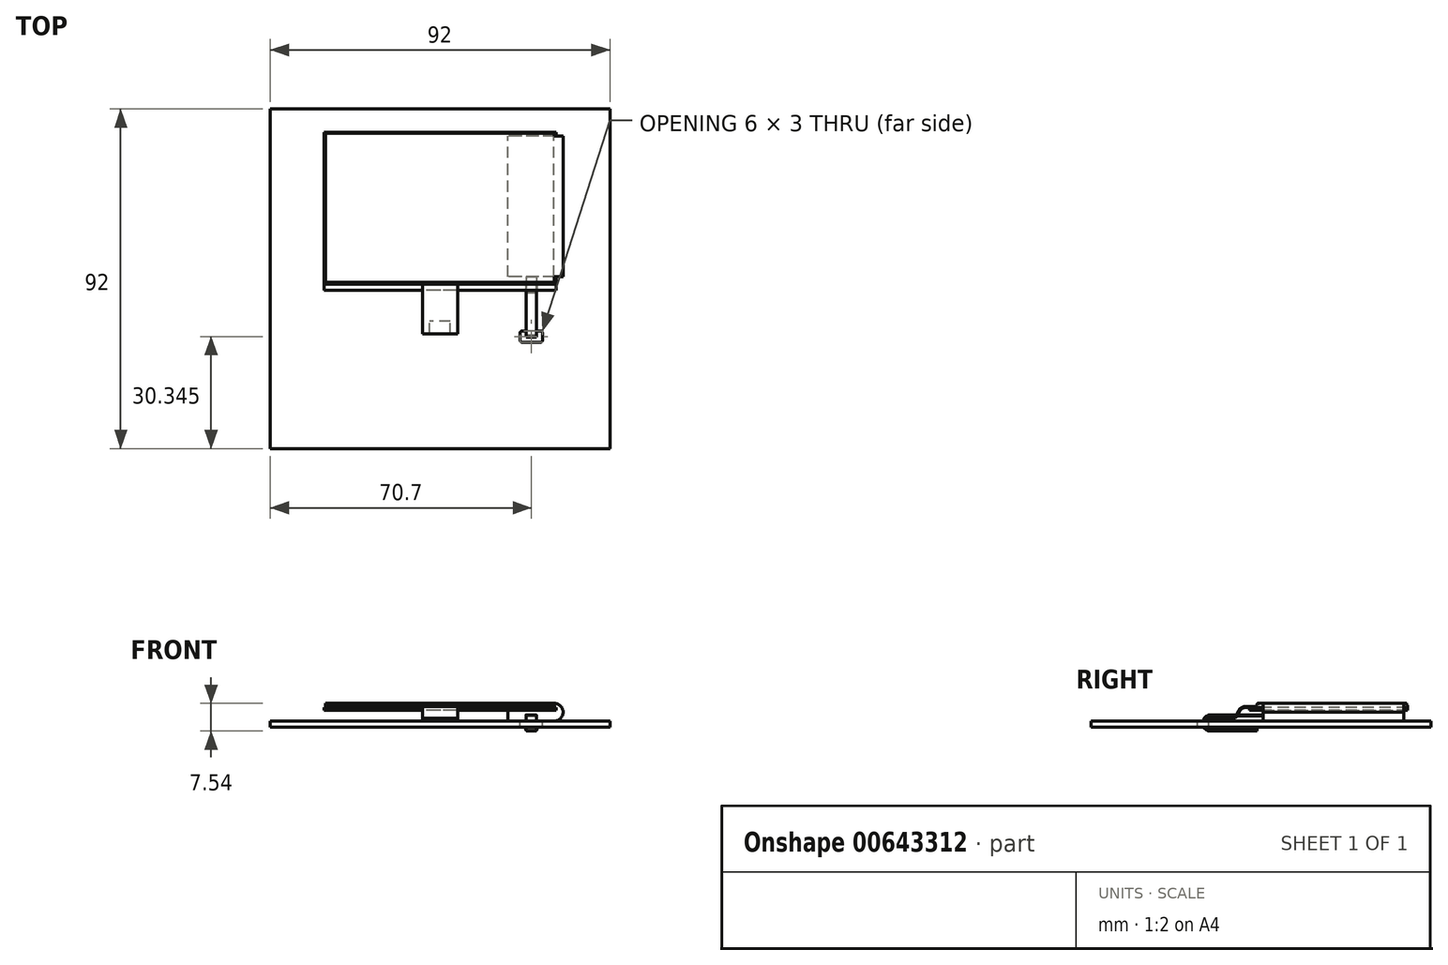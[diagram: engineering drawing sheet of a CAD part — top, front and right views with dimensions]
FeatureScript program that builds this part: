
annotation { "Feature Type Name" : "Feature", "Feature Type Description" : "" }
export const myFeature = defineFeature(function(context is Context, id is Id, definition is map)
    precondition{}
    {
        {
            var Q0;
            Q0=qCreatedBy(makeId("Top.planeOp"),FACE);
            var sketch = newSketch(context, id + "F0", { "sketchPlane" : qUnion([Q0])});
            skLineSegment(sketch, "E0.bottom", {"start": v(31.4, 21.41) * mm, "end": v(-31.4, 21.41) * mm});
            skLineSegment(sketch, "E0.top", {"start": v(31.4, -21.41) * mm, "end": v(-31.4, -21.41) * mm});
            skLineSegment(sketch, "E0.left", {"start": v(31.4, 21.41) * mm, "end": v(31.4, -21.41) * mm});
            skLineSegment(sketch, "E0.right", {"start": v(-31.4, 21.41) * mm, "end": v(-31.4, -21.41) * mm});
            skPoint(sketch, "E0.middle", {"position": v(0, 0) * mm});
            skSolve(sketch);
        }
        {
            var Q0;
            Q0=makeQuery(id+"F0.imprint","IMPRINT",FACE,{"disambiguationData":[TD([[makeQuery(id+"F0.imprint","IMPRINT",EDGE,{"derivedFrom":sQuery(id+"F0.wireOp",EDGE,"E0.bottom")}),1.0]])]});
            extrude(context, id + "F1", {"entities" : qUnion([Q0]), "depth" : (0.7 + 0.1) * mm, "offsetDistance" : 25 * mm});
        }
        {
            var Q0;
            Q0=makeQuery(id+"F1.opExtrude","CAP_FACE",FACE,{"disambiguationData":[OSD([sQuery(id+"F0.wireOp",EDGE,"E0.bottom"),sQuery(id+"F0.wireOp",EDGE,"E0.top"),sQuery(id+"F0.wireOp",EDGE,"E0.left"),sQuery(id+"F0.wireOp",EDGE,"E0.right")])],"isStart":true});
            var sketch = newSketch(context, id + "F2", { "sketchPlane" : qUnion([Q0])});
            skLineSegment(sketch, "E1.bottom", {"start": v(33.35, 17.74) * mm, "end": v(18.35, 17.74) * mm});
            skLineSegment(sketch, "E1.top", {"start": v(33.35, -20.41) * mm, "end": v(18.35, -20.41) * mm});
            skLineSegment(sketch, "E1.left", {"start": v(33.35, 17.74) * mm, "end": v(33.35, -20.41) * mm});
            skLineSegment(sketch, "E1.right", {"start": v(18.35, 17.74) * mm, "end": v(18.35, -20.41) * mm});
            skSolve(sketch);
        }
        {
            var Q0;
            Q0=qSketchRegion(id+"F2",true);
            extrude(context, id + "F3", {"entities" : qUnion([Q0]), "operationType" : NewBodyOperationType.ADD, "depth" : 2.9 * mm, "offsetDistance" : 25 * mm});
        }
        {
            var Q0;
            {var subQ0=sQuery(id+"F0.wireOp",EDGE,"E0.right");var subQ1=sQuery(id+"F0.wireOp",EDGE,"E0.left");var subQ2=sQuery(id+"F0.wireOp",EDGE,"E0.top");var subQ3=sQuery(id+"F0.wireOp",EDGE,"E0.bottom");Q0=makeQuery(id+"FSjtb73LsPTqSAc_1.boolean.opBoolean","MERGE",FACE,{"derivedFrom":[makeQuery(id+"F1.opExtrude","CAP_FACE",FACE,{"disambiguationData":[OSD([subQ3,subQ2,subQ1,subQ0])],"isStart":false}),makeQuery(id+"FSjtb73LsPTqSAc_1.opExtrude","CAP_FACE",FACE,{"disambiguationData":[OSD([subQ3,subQ2,subQ1,subQ0])],"isStart":false})]});}
            var sketch = newSketch(context, id + "F4", { "sketchPlane" : qUnion([Q0])});
            skLineSegment(sketch, "E2.bottom", {"start": v(-31, 21.4) * mm, "end": v(31, 21.41) * mm});
            skLineSegment(sketch, "E2.top", {"start": v(-31, -19.81) * mm, "end": v(31, -19.81) * mm});
            skLineSegment(sketch, "E2.left", {"start": v(-31, 21.4) * mm, "end": v(-31, -19.81) * mm});
            skLineSegment(sketch, "E2.right", {"start": v(31, 21.41) * mm, "end": v(31, -19.81) * mm});
            skLineSegment(sketch, "E3", {"start": v(0, 21.4) * mm, "end": v(0, -19.81) * mm, "construction": true});
            skSolve(sketch);
        }
        {
            var Q0;
            Q0=makeQuery(id+"F4.imprint","IMPRINT",FACE,{"disambiguationData":[TD([[makeQuery(id+"F4.imprint","IMPRINT",EDGE,{"derivedFrom":sQuery(id+"F4.wireOp",EDGE,"E2.bottom")}),1.0]])]});
            extrude(context, id + "F5", {"entities" : qUnion([Q0]), "operationType" : NewBodyOperationType.ADD, "depth" : 0.6 * mm, "offsetDistance" : 25 * mm});
        }
        {
            var Q0;
            Q0=makeQuery(id+"F5.opExtrude","CAP_FACE",FACE,{"disambiguationData":[OSD([sQuery(id+"F4.wireOp",EDGE,"E2.bottom"),sQuery(id+"F4.wireOp",EDGE,"E2.top"),sQuery(id+"F4.wireOp",EDGE,"E2.left"),sQuery(id+"F4.wireOp",EDGE,"E2.right")])],"isStart":false});
            var sketch = newSketch(context, id + "F6", { "sketchPlane" : qUnion([Q0])});
            skLineSegment(sketch, "E4.bottom", {"start": v(-31, 21.11) * mm, "end": v(31, 21.11) * mm});
            skLineSegment(sketch, "E4.top", {"start": v(-31, -19.31) * mm, "end": v(31, -19.31) * mm});
            skLineSegment(sketch, "E4.left", {"start": v(-31, 21.11) * mm, "end": v(-31, -19.31) * mm});
            skLineSegment(sketch, "E4.right", {"start": v(31, 21.11) * mm, "end": v(31, -19.31) * mm});
            skLineSegment(sketch, "E5", {"start": v(0, 21.11) * mm, "end": v(0, -19.31) * mm, "construction": true});
            skSolve(sketch);
        }
        {
            var Q0;
            Q0=makeQuery(id+"F6.imprint","IMPRINT",FACE,{"disambiguationData":[TD([[makeQuery(id+"F6.imprint","IMPRINT",EDGE,{"derivedFrom":sQuery(id+"F6.wireOp",EDGE,"E4.bottom")}),-1.0]])]});
            extrude(context, id + "F7", {"entities" : qUnion([Q0]), "operationType" : NewBodyOperationType.ADD, "depth" : (1.95 - 1.41) * mm, "offsetDistance" : 25 * mm});
        }
        {
            var Q0;
            Q0=makeQuery(id+"F7.opExtrude","CAP_FACE",FACE,{"disambiguationData":[OSD([sQuery(id+"F6.wireOp",EDGE,"E4.bottom"),sQuery(id+"F6.wireOp",EDGE,"E4.top"),sQuery(id+"F6.wireOp",EDGE,"E4.left"),sQuery(id+"F6.wireOp",EDGE,"E4.right")])],"isStart":false});
            var sketch = newSketch(context, id + "F8", { "sketchPlane" : qUnion([Q0])});
            skLineSegment(sketch, "E6.bottom", {"start": v(33.35, 20.41) * mm, "end": v(-31, 20.4) * mm});
            skLineSegment(sketch, "E6.top", {"start": v(33.35, -17.74) * mm, "end": v(-31, -17.74) * mm});
            skLineSegment(sketch, "E6.left", {"start": v(-31, 20.41) * mm, "end": v(-31, -17.74) * mm});
            skLineSegment(sketch, "E6.right", {"start": v(33.35, 20.41) * mm, "end": v(33.35, -17.74) * mm});
            skSolve(sketch);
        }
        {
            var Q0;
            Q0=makeQuery(id+"F8.imprint","IMPRINT",FACE,{"disambiguationData":[TD([[makeQuery(id+"F8.imprint","IMPRINT",EDGE,{"derivedFrom":sQuery(id+"F8.wireOp",EDGE,"E6.bottom")}),1.0]])]});
            var Q1;
            Q1=makeQuery(id+"F3.opExtrude","CAP_FACE",FACE,{"disambiguationData":[OSD([sQuery(id+"F2.wireOp",EDGE,"E1.bottom"),sQuery(id+"F2.wireOp",EDGE,"E1.top"),sQuery(id+"F2.wireOp",EDGE,"E1.left"),sQuery(id+"F2.wireOp",EDGE,"E1.right")])],"isStart":true});
            extrude(context, id + "F9", {"entities" : qUnion([Q0]), "operationType" : NewBodyOperationType.ADD, "endBound" : BoundingType.UP_TO_SURFACE, "oppositeDirection" : true, "depth" : 25 * mm, "endBoundEntityFace" : qUnion([Q1]), "offsetDistance" : 25 * mm});
        }
        {
            var Q0;
            Q0=makeQuery(id+"F9.opExtrude","CAP_EDGE",EDGE,{"disambiguationData":[OSD([sQuery(id+"F8.wireOp",EDGE,"E6.right")])],"isStart":true});
            var Q1;
            Q1=makeQuery(id+"F3.opExtrude","CAP_EDGE",EDGE,{"disambiguationData":[OSD([sQuery(id+"F2.wireOp",EDGE,"E1.left")])],"isStart":false});
            fillet(context, id + "F10", {"entities" : qUnion([Q0, Q1]), "radius" : 2.5 * mm, "tangentPropagation" : true, "allowEdgeOverflow" : false});
        }
        {
            var Q0;
            Q0=makeQuery(id+"F9.boolean.opBoolean","MERGE",FACE,{"derivedFrom":[makeQuery(id+"F3.opExtrude","SWEPT_FACE",FACE,{"disambiguationData":[OSD([sQuery(id+"F2.wireOp",EDGE,"E1.bottom")])]}),makeQuery(id+"F9.opExtrude","SWEPT_FACE",FACE,{"disambiguationData":[OSD([sQuery(id+"F8.wireOp",EDGE,"E6.top")])]})]});
            var sketch = newSketch(context, id + "F11", { "sketchPlane" : qUnion([Q0])});
            skLineSegment(sketch, "E7.bottom", {"start": v(23.3, -1.2) * mm, "end": v(26.1, -1.2) * mm});
            skLineSegment(sketch, "E7.top", {"start": v(23.3, -1.5) * mm, "end": v(26.1, -1.5) * mm});
            skLineSegment(sketch, "E7.left", {"start": v(23.3, -1.2) * mm, "end": v(23.3, -1.5) * mm});
            skLineSegment(sketch, "E7.right", {"start": v(26.1, -1.2) * mm, "end": v(26.1, -1.5) * mm});
            skPoint(sketch, "E8", {"position": v(24.7, -1.35) * mm});
            skLineSegment(sketch, "E9", {"start": v(24.7, -1.2) * mm, "end": v(24.7, -1.35) * mm, "construction": true});
            skLineSegment(sketch, "E10", {"start": v(24.7, -1.35) * mm, "end": v(26.1, -1.35) * mm, "construction": true});
            skSolve(sketch);
        }
        {
            var Q0;
            Q0=makeQuery(id+"F3.opExtrude","CAP_FACE",FACE,{"disambiguationData":[OSD([sQuery(id+"F2.wireOp",EDGE,"E1.bottom"),sQuery(id+"F2.wireOp",EDGE,"E1.top"),sQuery(id+"F2.wireOp",EDGE,"E1.left"),sQuery(id+"F2.wireOp",EDGE,"E1.right")])],"isStart":false});
            var sketch = newSketch(context, id + "F12", { "sketchPlane" : qUnion([Q0])});
            skLineSegment(sketch, "E11.bottom", {"start": v(46, 64.33) * mm, "end": v(-46, 64.33) * mm});
            skLineSegment(sketch, "E11.top", {"start": v(46, -27.67) * mm, "end": v(-46, -27.67) * mm});
            skLineSegment(sketch, "E11.left", {"start": v(46, 64.33) * mm, "end": v(46, -27.67) * mm});
            skLineSegment(sketch, "E11.right", {"start": v(-46, 64.33) * mm, "end": v(-46, -27.67) * mm});
            skPoint(sketch, "E11.middle", {"position": v(0, 64.33) * mm});
            skSolve(sketch);
        }
        {
            var Q0;
            Q0=qSketchRegion(id+"F12",true);
            extrude(context, id + "F13", {"entities" : qUnion([Q0]), "depth" : 1.6 * mm, "offsetDistance" : 25 * mm});
        }
        {
            var Q0;
            Q0=makeQuery(id+"F13.opExtrude","CAP_FACE",FACE,{"disambiguationData":[OSD([sQuery(id+"F12.wireOp",EDGE,"E11.bottom"),sQuery(id+"F12.wireOp",EDGE,"E11.top"),sQuery(id+"F12.wireOp",EDGE,"E11.left"),sQuery(id+"F12.wireOp",EDGE,"E11.right")])],"isStart":false});
            var sketch = newSketch(context, id + "F14", { "sketchPlane" : qUnion([Q0])});
            skPoint(sketch, "E12", {"position": v(24.7, 21.74) * mm});
            skSolve(sketch);
        }
        {
            var Q0;
            {var subQ3=sQuery(id+"F12.wireOp",EDGE,"E11.bottom");Q0=makeQuery(id+"F14.imprint","IMPRINT",FACE,{"disambiguationData":[TD([[makeQuery(id+"F14.imprint","IMPRINT",EDGE,{"derivedFrom":makeQuery(id+"F13.opExtrude","CAP_EDGE",EDGE,{"disambiguationData":[OSD([subQ3])],"isStart":false})}),1.0]])]});}
            var sketch = newSketch(context, id + "F15", { "sketchPlane" : qUnion([Q0])});
            skLineSegment(sketch, "E13.bottom", {"start": v(26.2, 19.35) * mm, "end": v(23.2, 19.35) * mm});
            skLineSegment(sketch, "E13.top", {"start": v(26.2, 22.25) * mm, "end": v(23.2, 22.25) * mm});
            skLineSegment(sketch, "E13.left", {"start": v(26.2, 19.35) * mm, "end": v(26.2, 22.25) * mm});
            skLineSegment(sketch, "E13.right", {"start": v(23.2, 19.35) * mm, "end": v(23.2, 22.25) * mm});
            skPoint(sketch, "E13.middle", {"position": v(24.7, 20.8) * mm});
            skSolve(sketch);
        }
        {
            var Q0;
            Q0=makeQuery(id+"F15.imprint","IMPRINT",FACE,{"disambiguationData":[TD([[makeQuery(id+"F15.imprint","IMPRINT",EDGE,{"derivedFrom":sQuery(id+"F15.wireOp",EDGE,"E13.bottom")}),-1.0]])]});
            extrude(context, id + "F16", {"entities" : qUnion([Q0]), "operationType" : NewBodyOperationType.ADD, "depth" : 0.79 * mm, "offsetDistance" : 25 * mm});
        }
        {
            var Q0;
            Q0=makeQuery(id+"F13.opExtrude","SWEPT_FACE",FACE,{"disambiguationData":[OSD([sQuery(id+"F12.wireOp",EDGE,"E11.right")])]});
            cPlane(context, id + "F17", {"entities" : qUnion([Q0]), "cplaneType" : CPlaneType.OFFSET, "offset" : (70.7) * mm, "oppositeDirection" : true, "width" : 150 * mm, "height" : 150 * mm});
        }
        {
            var Q0;
            Q0=qCreatedBy(id+"F17.planeOp",FACE);
            var sketch = newSketch(context, id + "F18", { "sketchPlane" : qUnion([Q0])});
            skLineSegment(sketch, "E14", {"start": v(17.74, -1.35) * mm, "end": v(31.94, -1.35) * mm});
            skArc(sketch, "E15", {"start": v(31.94, -5.44) * mm, "mid": v(33.98, -3.4) * mm, "end": v(31.94, -1.35) * mm});
            skLineSegment(sketch, "E16", {"start": v(31.94, -5.44) * mm, "end": v(19.35, -5.44) * mm});
            skSolve(sketch);
        }
        {
            var Q0;
            Q0=qSketchRegion(id+"F11",true);
            var Q1;
            Q1=qConstructionFilter(qBodyType(qCreatedBy(id+"F18",EDGE),BodyType.WIRE),ConstructionObject.NO);
            sweep(context, id + "F19", {"operationType" : NewBodyOperationType.ADD, "profiles" : qUnion([Q0]), "path" : qUnion([Q1])});
        }
        {
            var Q0;
            Q0=makeQuery(id+"F13.opExtrude","CAP_FACE",FACE,{"disambiguationData":[OSD([sQuery(id+"F12.wireOp",EDGE,"E11.bottom"),sQuery(id+"F12.wireOp",EDGE,"E11.top"),sQuery(id+"F12.wireOp",EDGE,"E11.left"),sQuery(id+"F12.wireOp",EDGE,"E11.right")])],"isStart":true});
            var sketch = newSketch(context, id + "F20", { "sketchPlane" : qUnion([Q0])});
            skLineSegment(sketch, "E17.bottom", {"start": v(27.3, -32.48) * mm, "end": v(22.1, -32.48) * mm});
            skLineSegment(sketch, "E17.top", {"start": v(27.3, -35.48) * mm, "end": v(22.1, -35.48) * mm});
            skLineSegment(sketch, "E17.left", {"start": v(27.7, -32.88) * mm, "end": v(27.7, -35.08) * mm});
            skLineSegment(sketch, "E17.right", {"start": v(21.7, -32.88) * mm, "end": v(21.7, -35.08) * mm});
            skPoint(sketch, "E17.middle", {"position": v(24.7, -33.98) * mm});
            skPoint(sketch, "E18.visualSharp", {"position": v(21.7, -32.48) * mm});
            skArc(sketch, "E18.filletArc", {"start": v(22.1, -32.48) * mm, "mid": v(21.82, -32.6) * mm, "end": v(21.7, -32.88) * mm});
            skPoint(sketch, "E19.visualSharp", {"position": v(27.7, -32.48) * mm});
            skArc(sketch, "E19.filletArc", {"start": v(27.7, -32.88) * mm, "mid": v(27.58, -32.6) * mm, "end": v(27.3, -32.48) * mm});
            skPoint(sketch, "E20.visualSharp", {"position": v(27.7, -35.48) * mm});
            skArc(sketch, "E20.filletArc", {"start": v(27.3, -35.48) * mm, "mid": v(27.58, -35.37) * mm, "end": v(27.7, -35.08) * mm});
            skPoint(sketch, "E21.visualSharp", {"position": v(21.7, -35.48) * mm});
            skArc(sketch, "E21.filletArc", {"start": v(21.7, -35.08) * mm, "mid": v(21.82, -35.37) * mm, "end": v(22.1, -35.48) * mm});
            skSolve(sketch);
        }
        {
            var Q0;
            Q0=qSketchRegion(id+"F20",true);
            var Q1;
            Q1=makeQuery(id+"F13.opExtrude","CAP_FACE",FACE,{"disambiguationData":[OSD([sQuery(id+"F12.wireOp",EDGE,"E11.bottom"),sQuery(id+"F12.wireOp",EDGE,"E11.top"),sQuery(id+"F12.wireOp",EDGE,"E11.left"),sQuery(id+"F12.wireOp",EDGE,"E11.right")])],"isStart":false});
            extrude(context, id + "F21", {"entities" : qUnion([Q0]), "operationType" : NewBodyOperationType.REMOVE, "endBound" : BoundingType.UP_TO_SURFACE, "oppositeDirection" : true, "depth" : 25 * mm, "endBoundEntityFace" : qUnion([Q1]), "offsetDistance" : 25 * mm});
        }
        {
            var Q0;
            Q0=makeQuery(id+"F5.opExtrude","SWEPT_FACE",FACE,{"disambiguationData":[OSD([sQuery(id+"F4.wireOp",EDGE,"E2.top")])]});
            var sketch = newSketch(context, id + "F22", { "sketchPlane" : qUnion([Q0])});
            skLineSegment(sketch, "E22.bottom", {"start": v(4.75, 0.81) * mm, "end": v(-4.75, 0.8) * mm});
            skLineSegment(sketch, "E22.top", {"start": v(4.75, 1.11) * mm, "end": v(-4.75, 1.1) * mm});
            skLineSegment(sketch, "E22.left", {"start": v(4.75, 0.81) * mm, "end": v(4.75, 1.11) * mm});
            skLineSegment(sketch, "E22.right", {"start": v(-4.75, 0.8) * mm, "end": v(-4.75, 1.1) * mm});
            skPoint(sketch, "E22.middle", {"position": v(0, 0.96) * mm});
            skPoint(sketch, "E22.middle.positionSnap0", {"position": v(0, 0.8) * mm});
            skPoint(sketch, "E22.centerSnap0", {"position": v(0, 0.8) * mm});
            skSolve(sketch);
        }
        {
            var Q0;
            Q0=makeQuery(id+"F13.opExtrude","SWEPT_FACE",FACE,{"disambiguationData":[OSD([sQuery(id+"F12.wireOp",EDGE,"E11.left")])]});
            cPlane(context, id + "F23", {"entities" : qUnion([Q0]), "cplaneType" : CPlaneType.OFFSET, "offset" : 46 * mm, "oppositeDirection" : true, "width" : 150 * mm, "height" : 150 * mm});
        }
        {
            var Q0;
            Q0=qCreatedBy(id+"F23.planeOp",FACE);
            var sketch = newSketch(context, id + "F24", { "sketchPlane" : qUnion([Q0])});
            skLineSegment(sketch, "E23", {"start": v(-19.81, 0.96) * mm, "end": v(-21.41, 0.96) * mm});
            skLineSegment(sketch, "E24", {"start": v(-21.41, 0.96) * mm, "end": v(-22.21, 0.96) * mm});
            skLineSegment(sketch, "E25", {"start": v(-26.71, -2.2) * mm, "end": v(-33.26, -2.2) * mm});
            skLineSegment(sketch, "E26", {"start": v(-24.25, -0.18) * mm, "end": v(-24.67, -1.06) * mm});
            skLineSegment(sketch, "E27", {"start": v(-22.21, 0.96) * mm, "end": v(-22.45, 0.96) * mm});
            skLineSegment(sketch, "E28", {"start": v(-26.47, -2.2) * mm, "end": v(-26.71, -2.2) * mm});
            skPoint(sketch, "E29.visualSharp", {"position": v(-23.71, 0.96) * mm});
            skArc(sketch, "E29.filletArc", {"start": v(-22.45, 0.96) * mm, "mid": v(-23.51, 0.65) * mm, "end": v(-24.25, -0.18) * mm});
            skPoint(sketch, "E30.visualSharp", {"position": v(-25.21, -2.2) * mm});
            skArc(sketch, "E30.filletArc", {"start": v(-26.47, -2.2) * mm, "mid": v(-25.4, -1.9) * mm, "end": v(-24.67, -1.06) * mm});
            skSolve(sketch);
        }
        {
            var Q0;
            Q0=makeQuery(id+"F22.imprint","IMPRINT",FACE,{"disambiguationData":[TD([[makeQuery(id+"F22.imprint","IMPRINT",EDGE,{"derivedFrom":sQuery(id+"F22.wireOp",EDGE,"E22.bottom")}),1.0]])]});
            var Q1;
            Q1=qConstructionFilter(qBodyType(qCreatedBy(id+"F24",EDGE),BodyType.WIRE),ConstructionObject.NO);
            sweep(context, id + "F25", {"operationType" : NewBodyOperationType.ADD, "profiles" : qUnion([Q0]), "path" : qUnion([Q1])});
        }
        {
            var Q0;
            Q0=makeQuery(id+"F13.opExtrude","CAP_FACE",FACE,{"disambiguationData":[OSD([sQuery(id+"F12.wireOp",EDGE,"E11.bottom"),sQuery(id+"F12.wireOp",EDGE,"E11.top"),sQuery(id+"F12.wireOp",EDGE,"E11.left"),sQuery(id+"F12.wireOp",EDGE,"E11.right")])],"isStart":true});
            var sketch = newSketch(context, id + "F26", { "sketchPlane" : qUnion([Q0])});
            skLineSegment(sketch, "E31.bottom", {"start": v(2.8, -33.26) * mm, "end": v(-2.8, -33.26) * mm});
            skLineSegment(sketch, "E31.top", {"start": v(2.8, -29.86) * mm, "end": v(-2.8, -29.86) * mm});
            skLineSegment(sketch, "E31.left", {"start": v(2.8, -33.26) * mm, "end": v(2.8, -29.86) * mm});
            skLineSegment(sketch, "E31.right", {"start": v(-2.8, -33.26) * mm, "end": v(-2.8, -29.86) * mm});
            skPoint(sketch, "E31.middle", {"position": v(0, -31.56) * mm});
            skSolve(sketch);
        }
        {
            var Q0;
            Q0=makeQuery(id+"F26.imprint","IMPRINT",FACE,{"disambiguationData":[TD([[makeQuery(id+"F26.imprint","IMPRINT",EDGE,{"derivedFrom":sQuery(id+"F26.wireOp",EDGE,"E31.bottom")}),-1.0]])]});
            extrude(context, id + "F27", {"entities" : qUnion([Q0]), "operationType" : NewBodyOperationType.ADD, "depth" : 0.55 * mm, "offsetDistance" : 25 * mm});
        }
    });
